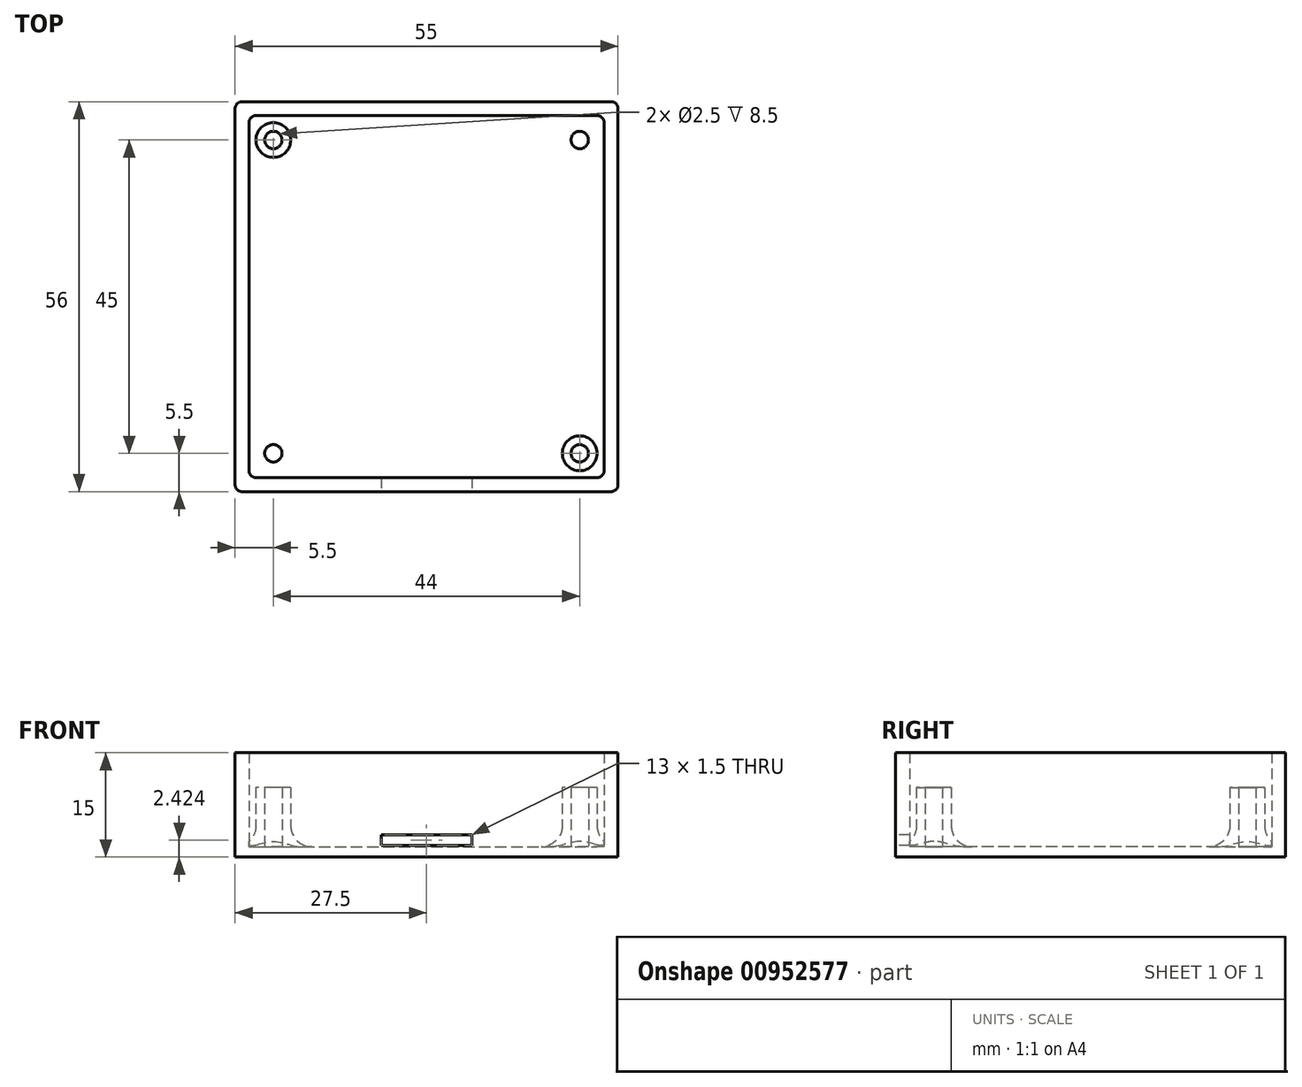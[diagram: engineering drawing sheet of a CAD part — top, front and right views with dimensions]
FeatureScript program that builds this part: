
annotation { "Feature Type Name" : "Feature", "Feature Type Description" : "" }
export const myFeature = defineFeature(function(context is Context, id is Id, definition is map)
    precondition{}
    {
        {
            var Q0;
            Q0=qCreatedBy(makeId("Top.planeOp"),FACE);
            var sketch = newSketch(context, id + "F0", { "sketchPlane" : qUnion([Q0])});
            skLineSegment(sketch, "E0.bottom", {"start": v(24.5, -26) * mm, "end": v(-24.5, -26) * mm});
            skLineSegment(sketch, "E0.top", {"start": v(24.5, 26) * mm, "end": v(-24.5, 26) * mm});
            skLineSegment(sketch, "E0.left", {"start": v(25.5, -25) * mm, "end": v(25.5, 25) * mm});
            skLineSegment(sketch, "E0.right", {"start": v(-25.5, -25) * mm, "end": v(-25.5, 25) * mm});
            skPoint(sketch, "E0.middle", {"position": v(0, 0) * mm});
            skLineSegment(sketch, "E1.0", {"start": v(27.5, -27) * mm, "end": v(27.5, 27) * mm});
            skLineSegment(sketch, "E1.1", {"start": v(26.5, -28) * mm, "end": v(-26.5, -28) * mm});
            skLineSegment(sketch, "E1.2", {"start": v(-27.5, -27) * mm, "end": v(-27.5, 27) * mm});
            skLineSegment(sketch, "E1.3", {"start": v(26.5, 28) * mm, "end": v(-26.5, 28) * mm});
            skPoint(sketch, "E2.visualSharp", {"position": v(-25.5, 26) * mm});
            skArc(sketch, "E2.filletArc", {"start": v(-24.5, 26) * mm, "mid": v(-25.2, 25.7) * mm, "end": v(-25.5, 25) * mm});
            skPoint(sketch, "E3.visualSharp", {"position": v(-27.5, 28) * mm});
            skArc(sketch, "E3.filletArc", {"start": v(-26.5, 28) * mm, "mid": v(-27.2, 27.7) * mm, "end": v(-27.5, 27) * mm});
            skPoint(sketch, "E4.visualSharp", {"position": v(-27.5, -28) * mm});
            skArc(sketch, "E4.filletArc", {"start": v(-27.5, -27) * mm, "mid": v(-27.2, -27.7) * mm, "end": v(-26.5, -28) * mm});
            skPoint(sketch, "E5.visualSharp", {"position": v(-25.5, -26) * mm});
            skArc(sketch, "E5.filletArc", {"start": v(-25.5, -25) * mm, "mid": v(-25.2, -25.7) * mm, "end": v(-24.5, -26) * mm});
            skPoint(sketch, "E6.visualSharp", {"position": v(25.5, -26) * mm});
            skArc(sketch, "E6.filletArc", {"start": v(24.5, -26) * mm, "mid": v(25.2, -25.7) * mm, "end": v(25.5, -25) * mm});
            skPoint(sketch, "E7.visualSharp", {"position": v(27.5, -28) * mm});
            skArc(sketch, "E7.filletArc", {"start": v(26.5, -28) * mm, "mid": v(27.2, -27.7) * mm, "end": v(27.5, -27) * mm});
            skPoint(sketch, "E8.visualSharp", {"position": v(25.5, 26) * mm});
            skArc(sketch, "E8.filletArc", {"start": v(25.5, 25) * mm, "mid": v(25.2, 25.7) * mm, "end": v(24.5, 26) * mm});
            skPoint(sketch, "E9.visualSharp", {"position": v(27.5, 28) * mm});
            skArc(sketch, "E9.filletArc", {"start": v(27.5, 27) * mm, "mid": v(27.2, 27.7) * mm, "end": v(26.5, 28) * mm});
            skCircle(sketch, "E10", {"center": v(-22, 22.5) * mm, "radius": 2.5 * mm});
            skCircle(sketch, "E11", {"center": v(-22, 22.5) * mm, "radius": 1.25 * mm});
            skCircle(sketch, "E12.MirrorC", {"center": v(22, 22.5) * mm, "radius": 1.25 * mm});
            skCircle(sketch, "E13.MirrorC", {"center": v(22, 22.5) * mm, "radius": 2.5 * mm});
            skCircle(sketch, "E14.MirrorC", {"center": v(-22, -22.5) * mm, "radius": 1.25 * mm});
            skCircle(sketch, "E15.MirrorC", {"center": v(-22, -22.5) * mm, "radius": 2.5 * mm});
            skCircle(sketch, "E16.MirrorC", {"center": v(22, -22.5) * mm, "radius": 2.5 * mm});
            skCircle(sketch, "E17.MirrorC", {"center": v(22, -22.5) * mm, "radius": 1.25 * mm});
            skSolve(sketch);
        }
        {
            var Q0;
            Q0=makeQuery(id+"F0.imprint","IMPRINT",FACE,{"disambiguationData":[TD([[makeQuery(id+"F0.imprint","IMPRINT",EDGE,{"derivedFrom":sQuery(id+"F0.wireOp",EDGE,"E0.bottom")}),-1.0]])]});
            var Q1;
            Q1=makeQuery(id+"F0.imprint","IMPRINT",FACE,{"disambiguationData":[TD([[makeQuery(id+"F0.imprint","IMPRINT",EDGE,{"derivedFrom":sQuery(id+"F0.wireOp",EDGE,"E0.bottom")}),1.0]])]});
            var Q2;
            Q2=makeQuery(id+"F0.imprint","IMPRINT",FACE,{"disambiguationData":[TD([[makeQuery(id+"F0.imprint","IMPRINT",EDGE,{"derivedFrom":sQuery(id+"F0.wireOp",EDGE,"E14.MirrorC")}),-1.0]])]});
            var Q3;
            Q3=makeQuery(id+"F0.imprint","IMPRINT",FACE,{"disambiguationData":[TD([[makeQuery(id+"F0.imprint","IMPRINT",EDGE,{"derivedFrom":sQuery(id+"F0.wireOp",EDGE,"E14.MirrorC")}),1.0]])]});
            var Q4;
            Q4=makeQuery(id+"F0.imprint","IMPRINT",FACE,{"disambiguationData":[TD([[makeQuery(id+"F0.imprint","IMPRINT",EDGE,{"derivedFrom":sQuery(id+"F0.wireOp",EDGE,"E17.MirrorC")}),1.0]])]});
            var Q5;
            Q5=makeQuery(id+"F0.imprint","IMPRINT",FACE,{"disambiguationData":[TD([[makeQuery(id+"F0.imprint","IMPRINT",EDGE,{"derivedFrom":sQuery(id+"F0.wireOp",EDGE,"E16.MirrorC")}),1.0]])]});
            var Q6;
            Q6=makeQuery(id+"F0.imprint","IMPRINT",FACE,{"disambiguationData":[TD([[makeQuery(id+"F0.imprint","IMPRINT",EDGE,{"derivedFrom":sQuery(id+"F0.wireOp",EDGE,"E12.MirrorC")}),1.0]])]});
            var Q7;
            Q7=makeQuery(id+"F0.imprint","IMPRINT",FACE,{"disambiguationData":[TD([[makeQuery(id+"F0.imprint","IMPRINT",EDGE,{"derivedFrom":sQuery(id+"F0.wireOp",EDGE,"E12.MirrorC")}),-1.0]])]});
            var Q8;
            Q8=makeQuery(id+"F0.imprint","IMPRINT",FACE,{"disambiguationData":[TD([[makeQuery(id+"F0.imprint","IMPRINT",EDGE,{"derivedFrom":sQuery(id+"F0.wireOp",EDGE,"E11")}),1.0]])]});
            var Q9;
            Q9=makeQuery(id+"F0.imprint","IMPRINT",FACE,{"disambiguationData":[TD([[makeQuery(id+"F0.imprint","IMPRINT",EDGE,{"derivedFrom":sQuery(id+"F0.wireOp",EDGE,"E10")}),1.0]])]});
            extrude(context, id + "F1", {"entities" : qUnion([Q0, Q1, Q2, Q3, Q4, Q5, Q6, Q7, Q8, Q9]), "depth" : 1.5 * mm, "offsetDistance" : 25 * mm});
        }
        {
            var Q0;
            Q0=makeQuery(id+"F0.imprint","IMPRINT",FACE,{"disambiguationData":[TD([[makeQuery(id+"F0.imprint","IMPRINT",EDGE,{"derivedFrom":sQuery(id+"F0.wireOp",EDGE,"E0.bottom")}),1.0]])]});
            extrude(context, id + "F2", {"entities" : qUnion([Q0]), "operationType" : NewBodyOperationType.ADD, "depth" : 15 * mm, "offsetDistance" : 25 * mm});
        }
        {
            var Q0;
            Q0=makeQuery(id+"F0.imprint","IMPRINT",FACE,{"disambiguationData":[TD([[makeQuery(id+"F0.imprint","IMPRINT",EDGE,{"derivedFrom":sQuery(id+"F0.wireOp",EDGE,"E12.MirrorC")}),1.0]])]});
            var Q1;
            Q1=makeQuery(id+"F0.imprint","IMPRINT",FACE,{"disambiguationData":[TD([[makeQuery(id+"F0.imprint","IMPRINT",EDGE,{"derivedFrom":sQuery(id+"F0.wireOp",EDGE,"E10")}),1.0]])]});
            var Q2;
            Q2=makeQuery(id+"F0.imprint","IMPRINT",FACE,{"disambiguationData":[TD([[makeQuery(id+"F0.imprint","IMPRINT",EDGE,{"derivedFrom":sQuery(id+"F0.wireOp",EDGE,"E14.MirrorC")}),1.0]])]});
            var Q3;
            Q3=makeQuery(id+"F0.imprint","IMPRINT",FACE,{"disambiguationData":[TD([[makeQuery(id+"F0.imprint","IMPRINT",EDGE,{"derivedFrom":sQuery(id+"F0.wireOp",EDGE,"E16.MirrorC")}),1.0]])]});
            extrude(context, id + "F3", {"entities" : qUnion([Q0, Q1, Q2, Q3]), "operationType" : NewBodyOperationType.ADD, "depth" : 10 * mm, "offsetDistance" : 25 * mm});
        }
        {
            var Q0;
            Q0=makeQuery(id+"F3.boolean.opBoolean","INTERSECT",EDGE,{"derivedFrom":[makeQuery(id+"F1.opExtrude","CAP_FACE",FACE,{"disambiguationData":[OSD([sQuery(id+"F0.wireOp",EDGE,"E1.0"),sQuery(id+"F0.wireOp",EDGE,"E1.1"),sQuery(id+"F0.wireOp",EDGE,"E1.2"),sQuery(id+"F0.wireOp",EDGE,"E1.3"),sQuery(id+"F0.wireOp",EDGE,"E3.filletArc"),sQuery(id+"F0.wireOp",EDGE,"E4.filletArc"),sQuery(id+"F0.wireOp",EDGE,"E7.filletArc"),sQuery(id+"F0.wireOp",EDGE,"E9.filletArc")])],"isStart":false}),makeQuery(id+"F3.opExtrude","SWEPT_FACE",FACE,{"disambiguationData":[OSD([sQuery(id+"F0.wireOp",EDGE,"E16.MirrorC")])]})]});
            var Q1;
            Q1=makeQuery(id+"F3.boolean.opBoolean","INTERSECT",EDGE,{"derivedFrom":[makeQuery(id+"F1.opExtrude","CAP_FACE",FACE,{"disambiguationData":[OSD([sQuery(id+"F0.wireOp",EDGE,"E1.0"),sQuery(id+"F0.wireOp",EDGE,"E1.1"),sQuery(id+"F0.wireOp",EDGE,"E1.2"),sQuery(id+"F0.wireOp",EDGE,"E1.3"),sQuery(id+"F0.wireOp",EDGE,"E3.filletArc"),sQuery(id+"F0.wireOp",EDGE,"E4.filletArc"),sQuery(id+"F0.wireOp",EDGE,"E7.filletArc"),sQuery(id+"F0.wireOp",EDGE,"E9.filletArc")])],"isStart":false}),makeQuery(id+"F3.opExtrude","SWEPT_FACE",FACE,{"disambiguationData":[OSD([sQuery(id+"F0.wireOp",EDGE,"E10")])]})]});
            var Q2;
            Q2=makeQuery(id+"F3.boolean.opBoolean","INTERSECT",EDGE,{"derivedFrom":[makeQuery(id+"F1.opExtrude","CAP_FACE",FACE,{"disambiguationData":[OSD([sQuery(id+"F0.wireOp",EDGE,"E1.0"),sQuery(id+"F0.wireOp",EDGE,"E1.1"),sQuery(id+"F0.wireOp",EDGE,"E1.2"),sQuery(id+"F0.wireOp",EDGE,"E1.3"),sQuery(id+"F0.wireOp",EDGE,"E3.filletArc"),sQuery(id+"F0.wireOp",EDGE,"E4.filletArc"),sQuery(id+"F0.wireOp",EDGE,"E7.filletArc"),sQuery(id+"F0.wireOp",EDGE,"E9.filletArc")])],"isStart":false}),makeQuery(id+"F3.opExtrude","SWEPT_FACE",FACE,{"disambiguationData":[OSD([sQuery(id+"F0.wireOp",EDGE,"E15.MirrorC")])]})]});
            var Q3;
            Q3=makeQuery(id+"F3.boolean.opBoolean","INTERSECT",EDGE,{"derivedFrom":[makeQuery(id+"F1.opExtrude","CAP_FACE",FACE,{"disambiguationData":[OSD([sQuery(id+"F0.wireOp",EDGE,"E1.0"),sQuery(id+"F0.wireOp",EDGE,"E1.1"),sQuery(id+"F0.wireOp",EDGE,"E1.2"),sQuery(id+"F0.wireOp",EDGE,"E1.3"),sQuery(id+"F0.wireOp",EDGE,"E3.filletArc"),sQuery(id+"F0.wireOp",EDGE,"E4.filletArc"),sQuery(id+"F0.wireOp",EDGE,"E7.filletArc"),sQuery(id+"F0.wireOp",EDGE,"E9.filletArc")])],"isStart":false}),makeQuery(id+"F3.opExtrude","SWEPT_FACE",FACE,{"disambiguationData":[OSD([sQuery(id+"F0.wireOp",EDGE,"E13.MirrorC")])]})]});
            fillet(context, id + "F4", {"entities" : qUnion([Q0, Q1, Q2, Q3]), "radius" : 3 * mm, "tangentPropagation" : true, "allowEdgeOverflow" : false});
        }
        {
            var Q0;
            {var subQ0=sQuery(id+"F0.wireOp",EDGE,"E1.1");Q0=makeQuery(id+"F2.boolean.opBoolean","MERGE",FACE,{"derivedFrom":[makeQuery(id+"F1.opExtrude","SWEPT_FACE",FACE,{"disambiguationData":[OSD([subQ0])]}),makeQuery(id+"F2.opExtrude","SWEPT_FACE",FACE,{"disambiguationData":[OSD([subQ0])]})]});}
            var sketch = newSketch(context, id + "F5", { "sketchPlane" : qUnion([Q0])});
            skLineSegment(sketch, "E18.bottom", {"start": v(6.5, 3.17) * mm, "end": v(-6.5, 3.17) * mm});
            skLineSegment(sketch, "E18.top", {"start": v(6.5, 1.67) * mm, "end": v(-6.5, 1.67) * mm});
            skLineSegment(sketch, "E18.left", {"start": v(6.5, 3.17) * mm, "end": v(6.5, 1.67) * mm});
            skLineSegment(sketch, "E18.right", {"start": v(-6.5, 3.17) * mm, "end": v(-6.5, 1.67) * mm});
            skPoint(sketch, "E18.middle", {"position": v(0, 2.42) * mm});
            skSolve(sketch);
        }
        {
            var Q0;
            Q0=makeQuery(id+"F5.imprint","IMPRINT",FACE,{"disambiguationData":[TD([[makeQuery(id+"F5.imprint","IMPRINT",EDGE,{"derivedFrom":sQuery(id+"F5.wireOp",EDGE,"E18.bottom")}),1.0]])]});
            extrude(context, id + "F6", {"entities" : qUnion([Q0]), "operationType" : NewBodyOperationType.REMOVE, "oppositeDirection" : true, "depth" : 5 * mm, "offsetDistance" : 25 * mm});
        }
    });
